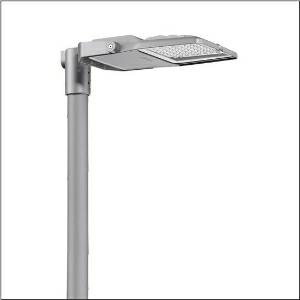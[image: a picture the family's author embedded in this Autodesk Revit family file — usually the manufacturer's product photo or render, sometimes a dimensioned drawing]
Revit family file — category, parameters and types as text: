
# Revit family: floodlight_fl_21_mini___pl64_5xa7776d4e3a_3ee3
name_source: partatom
category: Lighting Fixtures
units: mm (PartAtom-declared; Revit-internal decimal feet)

## family parameters
Cut with Voids When Loaded = No
Host = Face
Light Source = No
Part Type = Normal
Room Calculation Point = No
Round Connector Dimension = Use Diameter
Shared = No

## types (1)
- --- (1 x LED, 17960 lm, 142.9 W, 4000K)
    Apparent Load = 143 VA
    CIE Flux Codes = 28 80 98 100 100
    Color Rendering = 70
    Color Temperature = 4000K
    Default Elevation = 1800 mm
    Description = Floodlight FL 21 mini, floodlight, primary light control with lens, of PMMA, primary optical cover: protective disc, of toughened safety glass, transparent, light distribution: PL64, light emission: direct distribution, installation type: surface-mounted, LED, High Power LED, rated luminous flux: 17.960lm, luminous efficacy: 126lm/W, light colour: 740, colour temperature: 4000K, control gear: D4iSmart Interface (Zhaga), control: overheat protection, constant luminous flux control, time-dependent luminous flux control, flexible luminous flux parameterisation, pre-setting: logarithmic dimming characteristic, with terminal, 6-pole, mains connection: 220..240V, AC, 50/60Hz, start of lifetime: 143W, end of service life: 151W, reduction: 63W, mast bracket, of diecast aluminium, powder-coated, Siteco® metallic grey (DB 702S), corrosivity category C5 mid according to DIN EN ISO 12944, suitable for swimming pools, chlorine-resistant, sealing non-destructively replaceable, mast bracket, of steel, galvanised, powder-coated, Siteco® metallic grey (DB 702S), Smart Interface below and above, protection rating (complete): IP66, insulation class (complete): insulation class II (safety insulation), certification: CE, ENEC, VDE, protection symbol: D, impact resistance: IK08, permissible operating ambient temperature: -40..+40°C, permissible operating ambient temperature for outdoor applications: -40..+50°C, standard: DIN EN 12944, LABS conformity tested according to VDMA 24364:2018-05, packaging unit: 1 piece

Light Distribution: PL64
    Height = 70 mm
    Lamp = 1 x LED
    Lamp Light Flux = 17960 lm
    Lamp Power = 142.9 W
    Lamp count = 1
    Length = 485 mm
    Luminous efficacy = 126 lm/W
    Manufacturer = Siteco
    ModVariant = No
    Model = 5XA7776D4E3A
    Number of Poles = 1
    OnlyDefault = Yes
    Power Factor = 1
    Product Name = Floodlight FL 21 mini | PL64
    Product group = floodlight | pylon annexe
    ProductGroupID = 6201
    Protection Class = Protection class II
    Protection Degree = IP 66
    RLX_Detail_Level = 1
    RLX_Emergency_Light_Flux = 0 lm
    RLX_Emergency_Type = 0
    RLX_Emergency_Type_DB = No
    RlxData = <blob elided: 101217 chars, md5=d81ec465>
    Socket = socket
    Standby Power = 0 W
    System Light Flux = 17960 lm
    System Power = 143 W
    Type Comments = factory setting: luminous flux: 100 % | dim-lin: 254 | 730 mA
    Type Image = l_1007125.jpg
    URL = http://relux.com
    VarID = @adj_118571
    Voltage = 0 V
    Weight = 0.00 kg
    Width = 337 mm

## geometry (parser evidence)
native form markers: Blend x4, Sweep x12
no freeform markers — native parametric forms only
